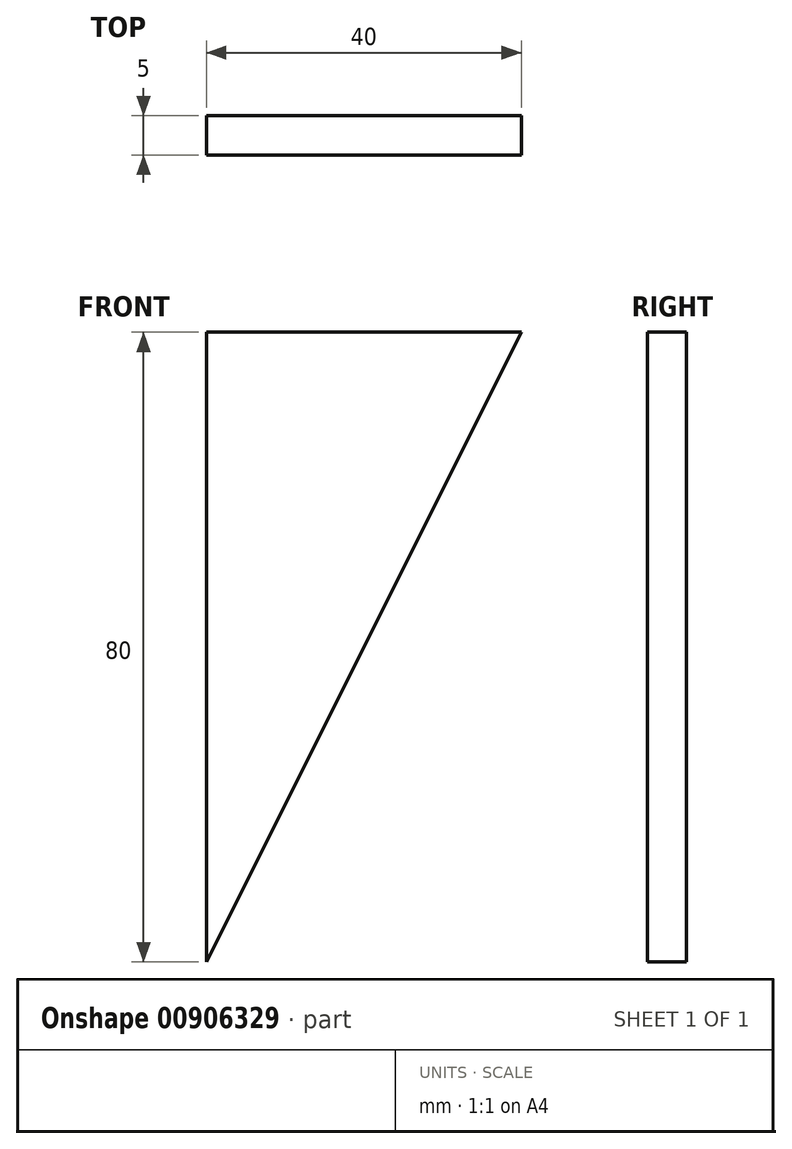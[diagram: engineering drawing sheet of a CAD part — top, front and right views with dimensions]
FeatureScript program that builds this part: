
annotation { "Feature Type Name" : "Feature", "Feature Type Description" : "" }
export const myFeature = defineFeature(function(context is Context, id is Id, definition is map)
    precondition{}
    {
        {
            var Q0;
            Q0=qCreatedBy(makeId("Front.planeOp"),FACE);
            var sketch = newSketch(context, id + "F0", { "sketchPlane" : qUnion([Q0])});
            skLineSegment(sketch, "E0", {"start": v(0, 0) * mm, "end": v(40, 80) * mm});
            skLineSegment(sketch, "E1", {"start": v(40, 80) * mm, "end": v(0, 80) * mm});
            skLineSegment(sketch, "E2", {"start": v(0, 80) * mm, "end": v(0, 0) * mm});
            skSolve(sketch);
        }
        {
            var Q0;
            Q0=makeQuery(id+"F0.imprint","IMPRINT",FACE,{"disambiguationData":[TD([[makeQuery(id+"F0.imprint","IMPRINT",EDGE,{"derivedFrom":sQuery(id+"F0.wireOp",EDGE,"E0")}),1.0]])]});
            extrude(context, id + "F1", {"entities" : qUnion([Q0]), "depth" : 5 * mm, "offsetDistance" : 25 * mm});
        }
    });
